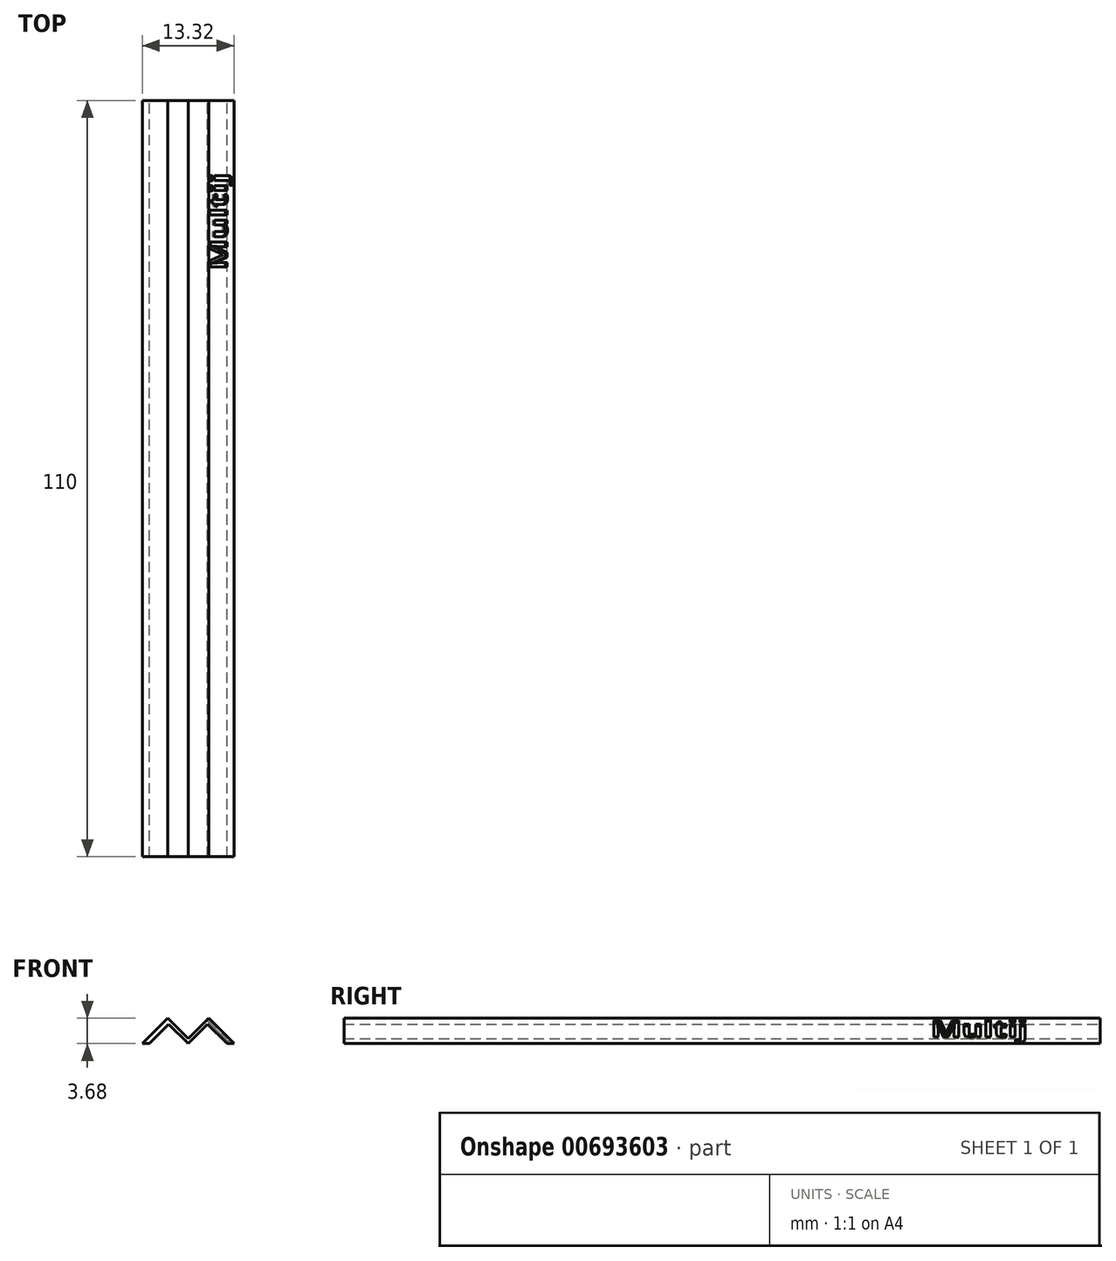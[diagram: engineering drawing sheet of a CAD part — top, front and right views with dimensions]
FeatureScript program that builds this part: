
annotation { "Feature Type Name" : "Feature", "Feature Type Description" : "" }
export const myFeature = defineFeature(function(context is Context, id is Id, definition is map)
    precondition{}
    {
        {
            var Q0;
            Q0=qCreatedBy(makeId("Front.planeOp"),FACE);
            var sketch = newSketch(context, id + "F0", { "sketchPlane" : qUnion([Q0])});
            skLineSegment(sketch, "E0", {"start": v(0, 0) * mm, "end": v(-2.83, 2.83) * mm});
            skLineSegment(sketch, "E1", {"start": v(-2.83, 2.83) * mm, "end": v(-5.66, 0) * mm});
            skLineSegment(sketch, "E2", {"start": v(-5.66, 0) * mm, "end": v(-6.66, 0) * mm});
            skLineSegment(sketch, "E3", {"start": v(0, 0) * mm, "end": v(0, 0.7) * mm, "construction": true});
            skLineSegment(sketch, "E4", {"start": v(0, 0.7) * mm, "end": v(-2.98, 3.68) * mm});
            skLineSegment(sketch, "E5", {"start": v(-2.98, 3.68) * mm, "end": v(-6.66, 0) * mm});
            skLineSegment(sketch, "E6.MirrorCS", {"start": v(0, 0) * mm, "end": v(2.83, 2.83) * mm});
            skLineSegment(sketch, "E7.MirrorCS", {"start": v(0, 0.7) * mm, "end": v(2.98, 3.68) * mm});
            skLineSegment(sketch, "E8.MirrorCS", {"start": v(2.98, 3.68) * mm, "end": v(6.66, 0) * mm});
            skLineSegment(sketch, "E9.MirrorCS", {"start": v(2.83, 2.83) * mm, "end": v(5.66, 0) * mm});
            skLineSegment(sketch, "E10.MirrorCS", {"start": v(5.66, 0) * mm, "end": v(6.66, 0) * mm});
            skSolve(sketch);
        }
        {
            var Q0;
            Q0=makeQuery(id+"F0.imprint","IMPRINT",FACE,{"disambiguationData":[TD([[makeQuery(id+"F0.imprint","IMPRINT",EDGE,{"derivedFrom":sQuery(id+"F0.wireOp",EDGE,"E0")}),-1.0]])]});
            extrude(context, id + "F1", {"entities" : qUnion([Q0]), "depth" : 110 * mm, "offsetDistance" : 25 * mm});
        }
        {
            var Q0;
            Q0=makeQuery(id+"F1.opExtrude","SWEPT_FACE",FACE,{"disambiguationData":[OSD([sQuery(id+"F0.wireOp",EDGE,"E8.MirrorCS")])]});
            var sketch = newSketch(context, id + "F2", { "sketchPlane" : qUnion([Q0])});
            skText(sketch, "E11", { "text": "Multij", "fontName": "OpenSans-Bold.ttf"});
            const initialGuessF2  = {"E11": [-0.02465, -0.00333, 1, 0, 0.00344]};
            skSetInitialGuess(sketch, initialGuessF2);
            skSolve(sketch);
        }
        {
            var Q0;
            Q0 = qSketchRegion(id + "F2", true);
            extrude(context, id + "F3", {"entities" : qUnion([Q0]), "operationType" : NewBodyOperationType.REMOVE, "oppositeDirection" : true, "depth" : 0.4 * mm, "offsetDistance" : 25 * mm});
        }
    });
